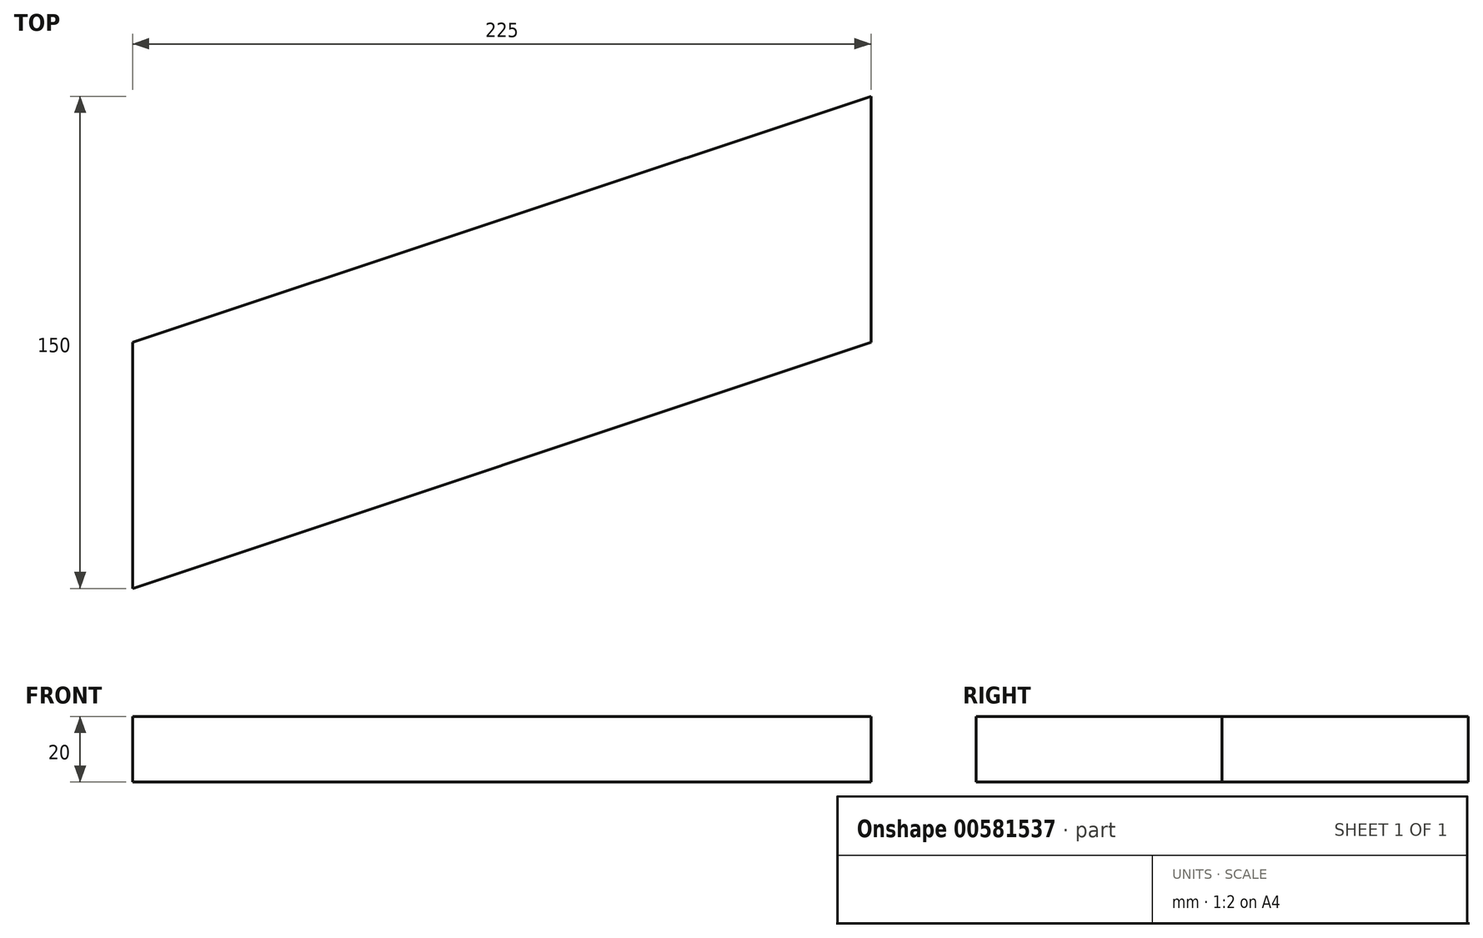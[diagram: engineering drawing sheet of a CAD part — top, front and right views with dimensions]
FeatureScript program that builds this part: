
annotation { "Feature Type Name" : "Feature", "Feature Type Description" : "" }
export const myFeature = defineFeature(function(context is Context, id is Id, definition is map)
    precondition{}
    {
        {
            var Q0;
            Q0=qCreatedBy(makeId("Top.planeOp"),FACE);
            var sketch = newSketch(context, id + "F0", { "sketchPlane" : qUnion([Q0])});
            skLineSegment(sketch, "E0", {"start": v(0, 0) * mm, "end": v(0, 75) * mm});
            skLineSegment(sketch, "E1", {"start": v(225, 150) * mm, "end": v(225, 75) * mm});
            skLineSegment(sketch, "E2", {"start": v(0, 0) * mm, "end": v(225, 75) * mm});
            skLineSegment(sketch, "E3", {"start": v(0, 75) * mm, "end": v(225, 150) * mm});
            skSolve(sketch);
        }
        {
            var Q0;
            Q0=makeQuery(id+"F0.imprint","IMPRINT",FACE,{"disambiguationData":[TD([[makeQuery(id+"F0.imprint","IMPRINT",EDGE,{"derivedFrom":sQuery(id+"F0.wireOp",EDGE,"E0")}),-1.0]])]});
            extrude(context, id + "F1", {"entities" : qUnion([Q0]), "depth" : 20 * mm, "offsetDistance" : 25 * mm});
        }
    });
